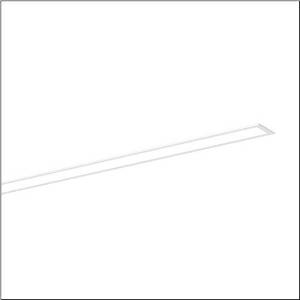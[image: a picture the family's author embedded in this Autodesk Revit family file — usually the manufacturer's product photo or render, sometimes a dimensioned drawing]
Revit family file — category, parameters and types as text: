
# Revit family: silica_21_51mx10da42wb
name_source: partatom
category: Lighting Fixtures
units: mm (PartAtom-declared; Revit-internal decimal feet)

## family parameters
Cut with Voids When Loaded = No
Host = Face
Light Source = No
Part Type = Normal
Room Calculation Point = No
Round Connector Dimension = Use Diameter
Shared = No

## types (1)
- --- (1 x LED, 2400 lm, 15.2 W, 4000K)
    Apparent Load = 15 VA
    CIE Flux Codes = 48 79 96 100 100
    Color Rendering = 80
    Color Temperature = 4000K
    Default Elevation = 1800 mm
    Description = Silica 21, office luminaire, primary optical cover: cover, of PMMA, opal, light emission: direct distribution, primary light characteristic: symmetric, installation type: recessed, LED, rated luminous flux: 2.400lm, luminous efficacy: 158lm/W, light colour: 840, colour temperature: 4000K, control gear: DALI 2, with terminal, 3+2-pole, max. 2.5mm², mains connection: 220..240V, AC, 50/60Hz, rated input power: 15.2W, luminaire housing, of aluminium, traffic white (RAL 9016), length: 1.228mm, width: 79mm, height: 53mm, protection rating (complete): IP20, insulation class (complete): insulation class I (protective earthing), certification: CE, ENEC, VDE, permissible operating ambient temperature: 0..+35°C, standard: EN 50419, packaging unit: 1 piece
    Height = 0 mm  [stored 0 ft]
    Lamp = 1 x LED
    Lamp Light Flux = 2400 lm
    Lamp Power = 15.2 W
    Lamp count = 1
    Length = 1227 mm
    Luminous efficacy = 158 lm/W
    Manufacturer = Siteco
    ModVariant = No
    Model = 51MX10DA42WB
    Mounting Place = Ceiling
    Mounting Type = Recessed
    Number of Poles = 1
    OnlyDefault = Yes
    Power Factor = 1
    Product Name = Silica 21
    Product group = office luminaire | ceiling recessed
    ProductGroupID = 400
    Protection Class = Protection class I
    Protection Degree = IP 20
    RLX_Detail_Level = 1
    RLX_Emergency_Light_Flux = 0 lm
    RLX_Emergency_Type = 0
    RLX_Emergency_Type_DB = No
    RlxData = <blob elided: 21053 chars, md5=a0834c93>
    Socket = socket
    Standby Power = 0 W
    System Light Flux = 2400 lm
    System Power = 15 W
    Type Comments = factory setting: luminous flux: 100 % | dim-lin: 254 | 218 mA
    Type Image = l_1335891.jpg
    URL = http://relux.com
    VarID = @adj_027713
    Voltage = 0 V
    Weight = 0.00 kg
    Width = 79 mm

note: [stored X ft] marks values corroborated as IEEE doubles in the binary element streams (Revit-internal decimal feet)

## geometry (parser evidence)
native form markers: Blend x4, Sweep x10
no freeform markers — native parametric forms only
